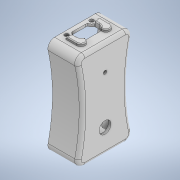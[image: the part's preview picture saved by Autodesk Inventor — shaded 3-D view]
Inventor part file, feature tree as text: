
AUTODESK INVENTOR PART (.ipt)
format: ipt  version: 2021 (Build 250183000, 183)  size: 437,760 bytes
history: native  units: mm
features: extrude x9, sketch x9, fillet x5, projected_geometry x3, mirror x2, shell x1
ambient origin geometry x8: Origin, YZ Plane, XZ Plane, XY Plane, X Axis, Y Axis, Z Axis, Center Point
bodies: Solid1 (feature_tree)
feature tree (29):
  extrude  "Extrusion1"  Depth=27.0mm
  extrude  "Extrusion5"  Depth=2.0mm
  fillet  "Fillet1"  Radius=1.5mm
  shell  "Shell1"  Thickness=3.8mm
  extrude  "Extrusion6"  Depth=4.0mm
  extrude  "Extrusion7"  Depth=2.4mm
  fillet  "Fillet3"  Radius=17.78mm
  extrude  "Extrusion8"  Depth=6.8mm TaperAngle=0.0deg
  extrude  "Extrusion9"  Depth=11.4mm
  extrude  "Extrusion10"  Depth=13.5mm
  extrude  "Extrusion11"  Depth=3.0mm
  fillet  "Fillet4"  Radius=39.37mm
  mirror  "Mirror1"
  fillet  "Fillet6"  Radius=7.1mm
  extrude  "Extrusion12"  Depth=0.5mm
  fillet  "Fillet7"  [1 undecoded]
  mirror  "Mirror2"
  sketch  "Sketch1"  dims[d0=18.0mm d1=27.0mm]
  sketch  "Sketch5"  dims[d2=58.0mm d3=0.0mm d4=2.0mm d5=1.5mm d26=3.8mm]
  sketch  "Sketch6"  dims[d27=0.0mm d28=0.0mm d29=4.0mm]
  sketch  "Sketch7"  dims[d33=5.0mm d34=2.4mm d36=17.78mm]
  sketch  "Sketch8"  dims[d37=45.72mm d38=6.8mm d39=0.0mm]
  sketch  "Sketch9"  dims[d40=3.0mm d41=11.4mm]
  sketch  "Sketch10"  dims[d42=8.2mm d43=13.5mm]
  sketch  "Sketch11"  dims[d44=1.5mm d45=0.0mm d46=3.0mm d47=39.37mm d48=7.1mm]
  sketch  "Sketch12"  dims[d49=2.0mm d50=10.795mm d51=0.0mm d52=0.0mm d53=2.4mm d54=2.5mm d55=15.0mm d56=0.0mm d57=0.0mm d58=5.0mm d59=5.0mm d60=1.5mm d61=0.0mm d62=5.0mm d63=5.0mm d64=1.5mm d65=0.0mm d66=1.0mm d68=0.5mm d69=5.0mm d70=5.0mm d71=1.5mm d72=0.0mm d73=0.5mm]
  projected_geometry  "Project Cut Edges6"
  projected_geometry  "Project Cut Edges7"
  projected_geometry  "Project Cut Edges8"
note: 1 required parameter value undecoded (feature->parameter linkage not recoverable at this tier; creation-order binding heuristic only, values carry confidence <= 0.55)
